# Revit family: Drain_Floor_16_Inch_Round_Top-Zurn-Z545-Heavy-Duty
name_source: partatom
category: Plumbing Fixtures
units: mm (PartAtom-declared; Revit-internal decimal feet)

## family parameters
Always vertical = Yes
Cut with Voids When Loaded = No
Maintain Annotation Orientation = No
OmniClass Number = 23.45.55.21
OmniClass Title = Drains (Wastes)
Part Type = Normal
Room Calculation Point = No
Round Connector Dimension = Use Radius
Shared = No
Work Plane-Based = No

## types (53) — shared parameters
Assembly Code = D2030300
CW Connection = No
Default Elevation = 4 "
Description = 16 [406] DIAMETER HEAVY DUTY DRAIN
Grate Open Area (Sq. In) = 45
HW Connection = No
Main Material = Iron - Zurn - Cast - Painted - Blue
Manufacturer = Zurn Water, LLC
Manufacurer Brand = Zurn
Modified Date = 12/05/2025
Product Documentation Link = https://files.zurn.com
Product Installation Sheet URL = https://www.zurn.com
Product Page URL = https://www.zurn.com
Product data url = https://www.bimobject.com
Top diameter = 16 "
Trap Primer = Yes
URL = www.zurn.com
Vent Connection = No
Waste Connection = Yes
zero-valued in all types: CWFU, HWFU, WFU

## per-type parameters (varying)
| type | A_ Pipe Size (Actual-Inner) | A_ Pipe Size (Actual-Outer) | A_ Pipe Size (Nominal) | Approx. Weight (Lbs) | Connector Radius | E_ Body Height | Frame Height | Grater Material | Type Comments | ZN-Top |
| Z545-3IC | 3.068 " | 3.5 " | 3 " | 69 " | 1.5 " | 5.25 " | 3.5 " | Iron - Zurn - Cast - Painted - Blue | Z545-3 Inch Inside Caulk Outlet | No |
| Z545-4IC | 4.026 " | 4.5 " | 4 " | 69 " | 2 " | 5.25 " | 3.5 " | Iron - Zurn - Cast - Painted - Blue | Z545-4 Inch Inside Caulk Outlet | No |
| Z545-2IP | 2.067 " | 2.375 " | 2 " | 69 " | 1 " | 3.75 " | 3.5 " | Iron - Zurn - Cast - Painted - Blue | Z545-2 Inch Threaded Outlet | No |
| Z545-3IP | 3.068 " | 3.5 " | 3 " | 69 " | 1.5 " | 3.75 " | 3.5 " | Iron - Zurn - Cast - Painted - Blue | Z545-3 Inch Threaded Outlet | No |
| Z545-4IP | 4.026 " | 4.5 " | 4 " | 69 " | 2 " | 3.75 " | 3.5 " | Iron - Zurn - Cast - Painted - Blue | Z545-4 Inch Threaded Outlet | No |
| Z545-6IP | 6.065 " | 6.625 " | 6 " | 69 " | 3 " | 3.75 " | 3.5 " | Iron - Zurn - Cast - Painted - Blue | Z545-6 Inch Threaded Outlet | No |
| Z545-8IP | 7.981 " | 8.625 " | 8 " | 71 " | 4 " | 3.75 " | 3.5 " | Iron - Zurn - Cast - Painted - Blue | Z545-8 Inch Threaded Outlet | No |
| Z545-10IP | 9.87 " | 10.13 " | 10 " | 70 " | 5 " | 3.75 " | 3.5 " | Iron - Zurn - Cast - Painted - Blue | Z545-10 Inch Threaded Outlet | No |
| Z545-2NH | 2.067 " | 2.375 " | 2 " | 69 " | 1 " | 5.25 " | 3.5 " | Iron - Zurn - Cast - Painted - Blue | Z545-2 Inch No-Hub Outlet | No |
| Z545-3NH | 3.068 " | 3.5 " | 3 " | 69 " | 1.5 " | 5.25 " | 3.5 " | Iron - Zurn - Cast - Painted - Blue | Z545-3 Inch No-Hub Outlet | No |
| Z545-4NH | 4.026 " | 4.5 " | 4 " | 69 " | 2 " | 5.25 " | 3.5 " | Iron - Zurn - Cast - Painted - Blue | Z545-4 Inch No-Hub Outlet | No |
| Z545-6NH | 6.065 " | 6.625 " | 6 " | 69 " | 3 " | 5.25 " | 3.5 " | Iron - Zurn - Cast - Painted - Blue | Z545-6 Inch No-Hub Outlet | No |
| Z545-8NH | 7.981 " | 8.625 " | 8 " | 71 " | 4 " | 5.25 " | 3.5 " | Iron - Zurn - Cast - Painted - Blue | Z545-8 Inch No-Hub Outlet | No |
| Z545-10NH | 9.87 " | 10.13 " | 10 " | 70 " | 5 " | 3.75 " | 3.5 " | Iron - Zurn - Cast - Painted - Blue | Z545-10 Inch No-Hub Outlet | No |
| Z545-2NL | 2.067 " | 2.375 " | 2 " | 69 " | 1 " | 4.625 " | 3.5 " | Iron - Zurn - Cast - Painted - Blue | Z545-2 Inch Neo-Loc Outlet | No |
| Z545-3NL | 3.068 " | 3.5 " | 3 " | 69 " | 1.5 " | 4.625 " | 3.5 " | Iron - Zurn - Cast - Painted - Blue | Z545-3 Inch Neo-Loc Outlet | No |
| Z545-4NL | 4.026 " | 4.5 " | 4 " | 69 " | 2 " | 4.625 " | 3.5 " | Iron - Zurn - Cast - Painted - Blue | Z545-4 Inch Neo-Loc Outlet | No |
| ZN545-3IC | 3.068 " | 3.5 " | 3 " | 69 " | 1.5 " | 5.25 " | 3.688 " | Bronze - Zurn - Polished Nickel | ZN545-3 Inch Inside Caulk Outlet with Polished Nickel Bronze Top | Yes |
| ZN545-4IC | 4.026 " | 4.5 " | 4 " | 69 " | 2 " | 5.25 " | 3.688 " | Bronze - Zurn - Polished Nickel | ZN545-4 Inch Inside Caulk Outlet with Polished Nickel Bronze Top | Yes |
| ZN545-6IC | 6.065 " | 6.625 " | 6 " | 69 " | 3 " | 5.25 " | 3.688 " | Bronze - Zurn - Polished Nickel | ZN545-6 Inch Inside Caulk Outlet with Polished Nickel Bronze Top | Yes |
| ZN545-2IP | 2.067 " | 2.375 " | 2 " | 69 " | 1 " | 3.75 " | 3.688 " | Bronze - Zurn - Polished Nickel | ZN545-2 Inch Threaded Outlet with Polished Nickel Bronze Top | Yes |
| ZN545-3IP | 3.068 " | 3.5 " | 3 " | 69 " | 1.5 " | 3.75 " | 3.688 " | Bronze - Zurn - Polished Nickel | ZN545-3 Inch Threaded Outlet with Polished Nickel Bronze Top | Yes |
| ZN545-4IP | 4.026 " | 4.5 " | 4 " | 69 " | 2 " | 3.75 " | 3.688 " | Bronze - Zurn - Polished Nickel | ZN545-4 Inch Threaded Outlet with Polished Nickel Bronze Top | Yes |
| ZN545-6IP | 6.065 " | 6.625 " | 6 " | 71 " | 3 " | 3.75 " | 3.688 " | Bronze - Zurn - Polished Nickel | ZN545-6 Inch Threaded Outlet with Polished Nickel Bronze Top | Yes |
| ZN545-8IP | 7.981 " | 8.625 " | 8 " | 70 " | 4 " | 3.75 " | 3.688 " | Bronze - Zurn - Polished Nickel | ZN545-8 Inch Threaded Outlet with Polished Nickel Bronze Top | Yes |
| ZN545-10IP | 9.87 " | 10.13 " | 10 " | 69 " | 5 " | 3.75 " | 3.688 " | Bronze - Zurn - Polished Nickel | ZN545-10 Inch Threaded Outlet with Polished Nickel Bronze Top | Yes |
| ZN545-2NH | 2.067 " | 2.375 " | 2 " | 69 " | 1 " | 5.25 " | 3.688 " | Bronze - Zurn - Polished Nickel | ZN545-2 Inch No-Hub Outlet with Polished Nickel Bronze Top | Yes |
| ZN545-3NH | 3.068 " | 3.5 " | 3 " | 69 " | 1.5 " | 5.25 " | 3.688 " | Bronze - Zurn - Polished Nickel | ZN545-3 Inch No-Hub Outlet with Polished Nickel Bronze Top | Yes |
| ZN545-4NH | 4.026 " | 4.5 " | 4 " | 69 " | 2 " | 5.25 " | 3.688 " | Bronze - Zurn - Polished Nickel | ZN545-4 Inch No-Hub Outlet with Polished Nickel Bronze Top | Yes |
| ZN545-6NH | 6.065 " | 6.625 " | 6 " | 71 " | 3 " | 5.25 " | 3.688 " | Bronze - Zurn - Polished Nickel | ZN545-6 Inch No-Hub Outlet with Polished Nickel Bronze Top | Yes |
| ZN545-8NH | 7.981 " | 8.625 " | 8 " | 70 " | 4 " | 5.25 " | 3.688 " | Bronze - Zurn - Polished Nickel | ZN545-8 Inch No-Hub Outlet with Polished Nickel Bronze Top | Yes |
| ZN545-10NH | 9.87 " | 10.13 " | 10 " | 69 " | 5 " | 5.25 " | 3.688 " | Bronze - Zurn - Polished Nickel | ZN545-10 Inch No-Hub Outlet with Polished Nickel Bronze Top | Yes |
| ZN545-2NL | 2.067 " | 2.375 " | 2 " | 69 " | 1 " | 4.625 " | 3.688 " | Bronze - Zurn - Polished Nickel | ZN545-2 Inch Neo-Loc Outlet with Polished Nickel Bronze Top | Yes |
| ZN545-3NL | 3.068 " | 3.5 " | 3 " | 69 " | 1.5 " | 4.625 " | 3.688 " | Bronze - Zurn - Polished Nickel | ZN545-3 Inch Neo-Loc Outlet with Polished Nickel Bronze Top | Yes |
| ZN545-4NL | 4.026 " | 4.5 " | 4 " | 69 " | 2 " | 4.625 " | 3.688 " | Bronze - Zurn - Polished Nickel | ZN545-4 Inch Neo-Loc Outlet with Polished Nickel Bronze Top | Yes |
| ZB545-3IC | 3.068 " | 3.5 " | 3 " | 69 " | 1.5 " | 5.25 " | 3.688 " | Bronze - Zurn - Polished | ZB545-3 Inch Inside Caulk Outlet with Polished Bronze Top | Yes |
| ZB545-4IC | 4.026 " | 4.5 " | 4 " | 69 " | 2 " | 5.25 " | 3.688 " | Bronze - Zurn - Polished | ZB545-4 Inch Inside Caulk Outlet with Polished Bronze Top | Yes |
| ZB545-6IC | 6.065 " | 6.625 " | 6 " | 69 " | 3 " | 5.25 " | 3.688 " | Bronze - Zurn - Polished | ZB545-6 Inch Inside Caulk Outlet with Polished Bronze Top | Yes |
| ZB545-2IP | 2.067 " | 2.375 " | 2 " | 69 " | 1 " | 3.75 " | 3.688 " | Bronze - Zurn - Polished | ZB545-2 Inch Threaded Outlet with Polished Bronze Top | Yes |
| ZB545-3IP | 3.068 " | 3.5 " | 3 " | 69 " | 1.5 " | 3.75 " | 3.688 " | Bronze - Zurn - Polished | ZB545-3 Inch Threaded Outlet with Polished Bronze Top | Yes |
| ZB545-4IP | 4.026 " | 4.5 " | 4 " | 69 " | 2 " | 3.75 " | 3.688 " | Bronze - Zurn - Polished | ZB545-4 Inch Threaded Outlet with Polished Bronze Top | Yes |
| ZB545-6IP | 6.065 " | 6.625 " | 6 " | 71 " | 3 " | 3.75 " | 3.688 " | Bronze - Zurn - Polished | ZB545-6 Inch Threaded Outlet with Polished Bronze Top | Yes |
| ZB545-8IP | 7.981 " | 8.625 " | 8 " | 70 " | 4 " | 3.75 " | 3.688 " | Bronze - Zurn - Polished | ZB545-8 Inch Threaded Outlet with Polished Bronze Top | Yes |
| ZB545-10IP | 9.87 " | 10.13 " | 10 " | 69 " | 5 " | 3.75 " | 3.688 " | Bronze - Zurn - Polished | ZB545-10 Inch Threaded Outlet with Polished Bronze Top | Yes |
| ZB545-2NH | 2.067 " | 2.375 " | 2 " | 69 " | 1 " | 5.25 " | 3.688 " | Bronze - Zurn - Polished | ZB545-2 Inch No-Hub Outlet with Polished Bronze Top | Yes |
| ZB545-3NH | 3.068 " | 3.5 " | 3 " | 69 " | 1.5 " | 5.25 " | 3.688 " | Bronze - Zurn - Polished | ZB545-3 Inch No-Hub Outlet with Polished Bronze Top | Yes |
| ZB545-4NH | 4.026 " | 4.5 " | 4 " | 69 " | 2 " | 5.25 " | 3.688 " | Bronze - Zurn - Polished | ZB545-4 Inch No-Hub Outlet with Polished Bronze Top | Yes |
| ZB545-6NH | 6.065 " | 6.625 " | 6 " | 71 " | 3 " | 5.25 " | 3.688 " | Bronze - Zurn - Polished | ZB545-6 Inch No-Hub Outlet with Polished Bronze Top | Yes |
| ZB545-8NH | 7.981 " | 8.625 " | 8 " | 70 " | 4 " | 5.25 " | 3.688 " | Bronze - Zurn - Polished | ZB545-8 Inch No-Hub Outlet with Polished Bronze Top | Yes |
| ZB545-10NH | 9.87 " | 10.13 " | 10 " | 69 " | 5 " | 5.25 " | 3.688 " | Bronze - Zurn - Polished | ZB545-10 Inch No-Hub Outlet with Polished Bronze Top | Yes |
| ZB545-2NL | 2.067 " | 2.375 " | 2 " | 69 " | 1 " | 4.625 " | 3.688 " | Bronze - Zurn - Polished | ZB545-2 Inch Neo-Loc Outlet with Polished Bronze Top | Yes |
| ZB545-3NL | 3.068 " | 3.5 " | 3 " | 69 " | 1.5 " | 4.625 " | 3.688 " | Bronze - Zurn - Polished | ZB545-3 Inch Neo-Loc Outlet with Polished Bronze Top | Yes |
| ZB545-4NL | 4.026 " | 4.5 " | 4 " | 69 " | 2 " | 4.625 " | 3.688 " | Bronze - Zurn - Polished | ZB545-4 Inch Neo-Loc Outlet with Polished Bronze Top | Yes |

note: column(s) folded — value = type name in every type: Model

## geometry (parser evidence)
native form markers: Blend x8, Sweep x4
no freeform markers — native parametric forms only
